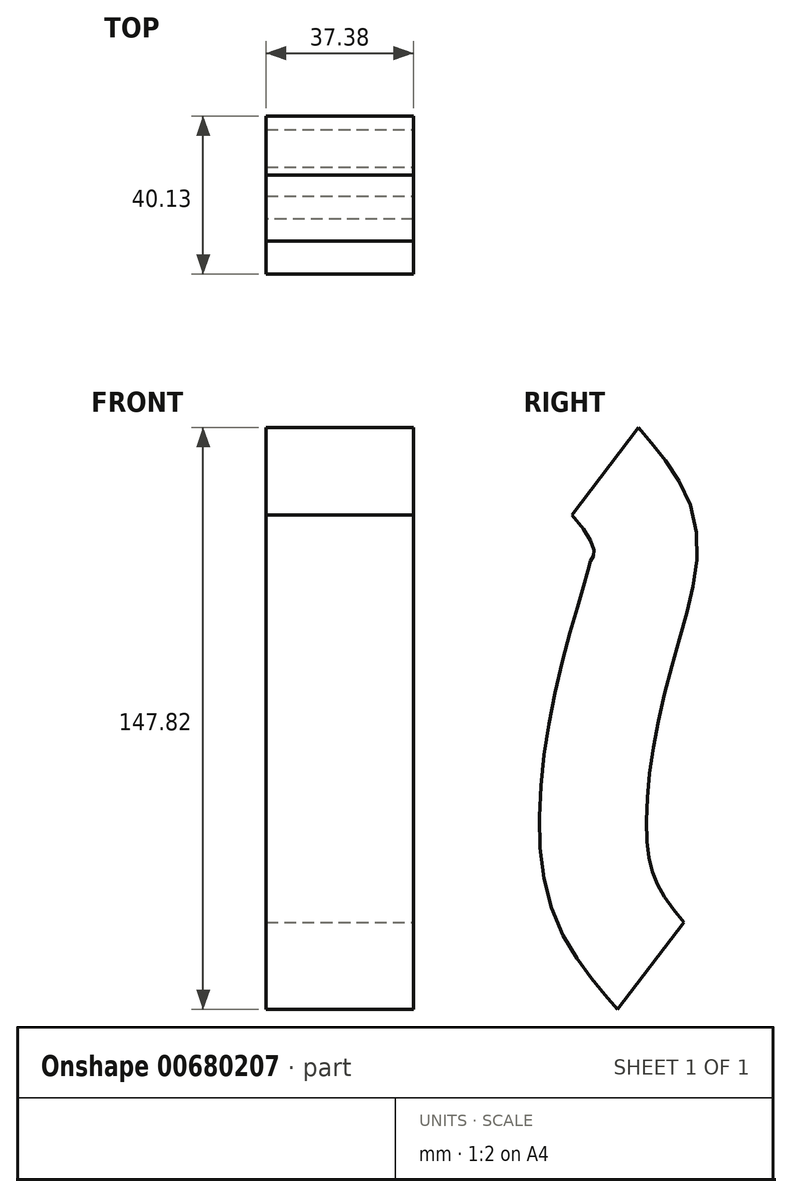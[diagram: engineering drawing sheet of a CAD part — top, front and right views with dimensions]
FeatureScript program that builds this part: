
annotation { "Feature Type Name" : "Feature", "Feature Type Description" : "" }
export const myFeature = defineFeature(function(context is Context, id is Id, definition is map)
    precondition{}
    {
        {
            var Q0;
            Q0=qCreatedBy(makeId("Top.planeOp"),FACE);
            var sketch = newSketch(context, id + "F0", { "sketchPlane" : qUnion([Q0])});
            skLineSegment(sketch, "E0.bottom", {"start": v(-48.41, -11.45) * mm, "end": v(-11.03, -11.45) * mm});
            skLineSegment(sketch, "E0.top", {"start": v(-48.41, -39.28) * mm, "end": v(-11.03, -39.28) * mm});
            skLineSegment(sketch, "E0.left", {"start": v(-48.41, -11.45) * mm, "end": v(-48.41, -39.28) * mm});
            skLineSegment(sketch, "E0.right", {"start": v(-11.03, -11.45) * mm, "end": v(-11.03, -39.28) * mm});
            skLineSegment(sketch, "E1.bottom", {"start": v(-24.79, 46.95) * mm, "end": v(26.23, 46.95) * mm});
            skLineSegment(sketch, "E1.top", {"start": v(-24.79, 12.75) * mm, "end": v(26.23, 12.75) * mm});
            skLineSegment(sketch, "E1.left", {"start": v(-24.79, 46.95) * mm, "end": v(-24.79, 12.75) * mm});
            skLineSegment(sketch, "E1.right", {"start": v(26.23, 46.95) * mm, "end": v(26.23, 12.75) * mm});
            skSolve(sketch);
        }
        {
            var Q0;
            Q0=qCreatedBy(makeId("Right.planeOp"),FACE);
            var sketch = newSketch(context, id + "F1", { "sketchPlane" : qUnion([Q0])});
            skFitSpline(sketch, "E2", {"points": [v(-23.95, 61.34) * mm, v(-13.22, 42.92) * mm, v(-20.1, 7.61) * mm, v(-24.55, -43.07) * mm, v(-12.36, -64.35) * mm], "startDerivative": vector(70.72, -83.17) * mm, "endDerivative": vector(69.31, -82.25) * mm});
            skFitSpline(sketch, "E3", {"points": [v(26.49, 59.27) * mm, v(39.86, 24.4) * mm, v(25.73, -28.89) * mm, v(36.9, -65.76) * mm], "startDerivative": vector(67.78, -103.92) * mm, "endDerivative": vector(58.96, -109.32) * mm});
            skSolve(sketch);
        }
        {
            var Q0;
            Q0=makeQuery(id+"F0.imprint","IMPRINT",FACE,{"disambiguationData":[TD([[makeQuery(id+"F0.imprint","IMPRINT",EDGE,{"derivedFrom":sQuery(id+"F0.wireOp",EDGE,"E0.bottom")}),-1.0]])]});
            var Q1;
            Q1=sQuery(id+"F1.wireOp",EDGE,"E2");
            sweep(context, id + "F2", {"profiles" : qUnion([Q0]), "path" : qUnion([Q1])});
        }
    });
